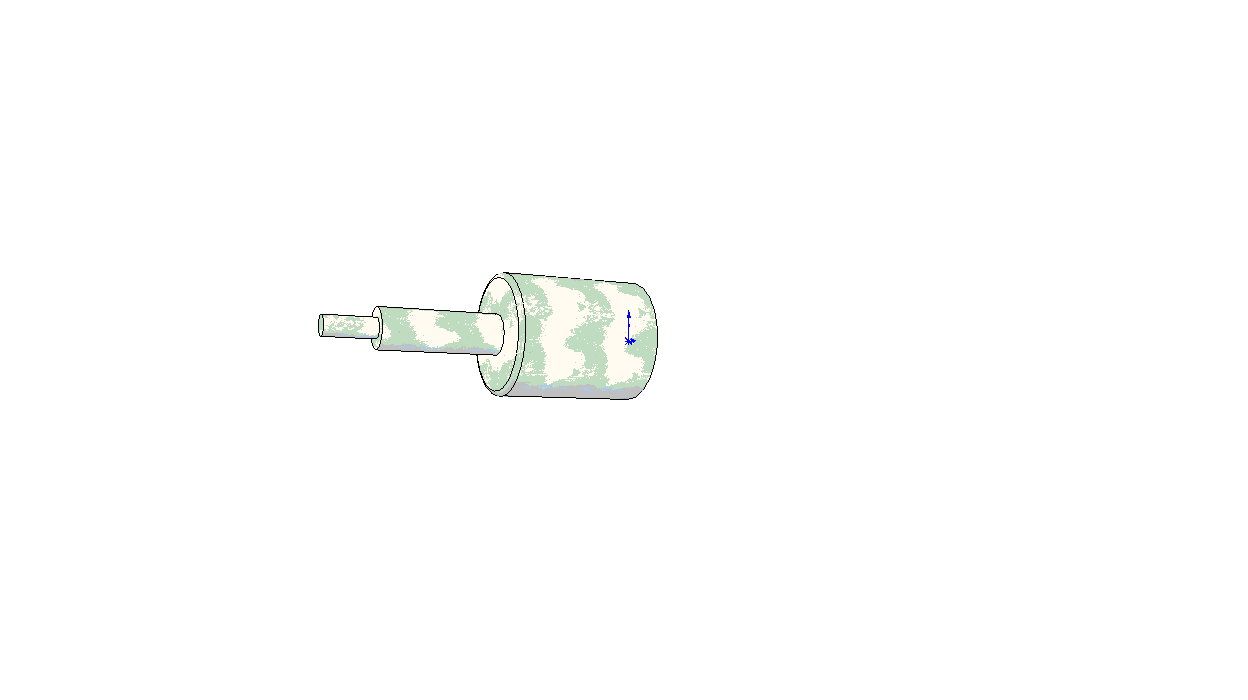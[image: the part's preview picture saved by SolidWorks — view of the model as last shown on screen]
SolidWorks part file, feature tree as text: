
SOLIDWORKS PART (.sldprt)
format: sldprt  version: not decoded by parser v0  size: 110,080 bytes
history: native  units: mm
features: plane x3, sketch x3, extrude x3, material x1, fillet x1 (+8 scaffold rows collapsed)
feature tree (19):
  scaffold x8  (default folders/planes/origin — collapsed)
  material  "Matériau <non spécifié>"
  plane  "Plan de face"
  plane  "Plan de dessus"
  plane  "Plan de droite"
  sketch  "Esquisse1"  dims[D1=~17.495755mm]
  extrude  "Extrusion1"  Depth=29.2mm
  fillet  "Congé1"  Radius=1mm
  sketch  "Esquisse2"  dims[D1=8.0mm]
  extrude  "Extrusion2"  Depth=23.43mm
  sketch  "Esquisse3"  dims[D1=~0.867422mm]
  extrude  "Extrusion3"  Depth=10mm
decode coverage: 7 of 7 modeling features carry decoded parameters
note: ~ marks probable driven/reference dimensions
note: suppression state not decoded; provenance and decode notes live in map.json
